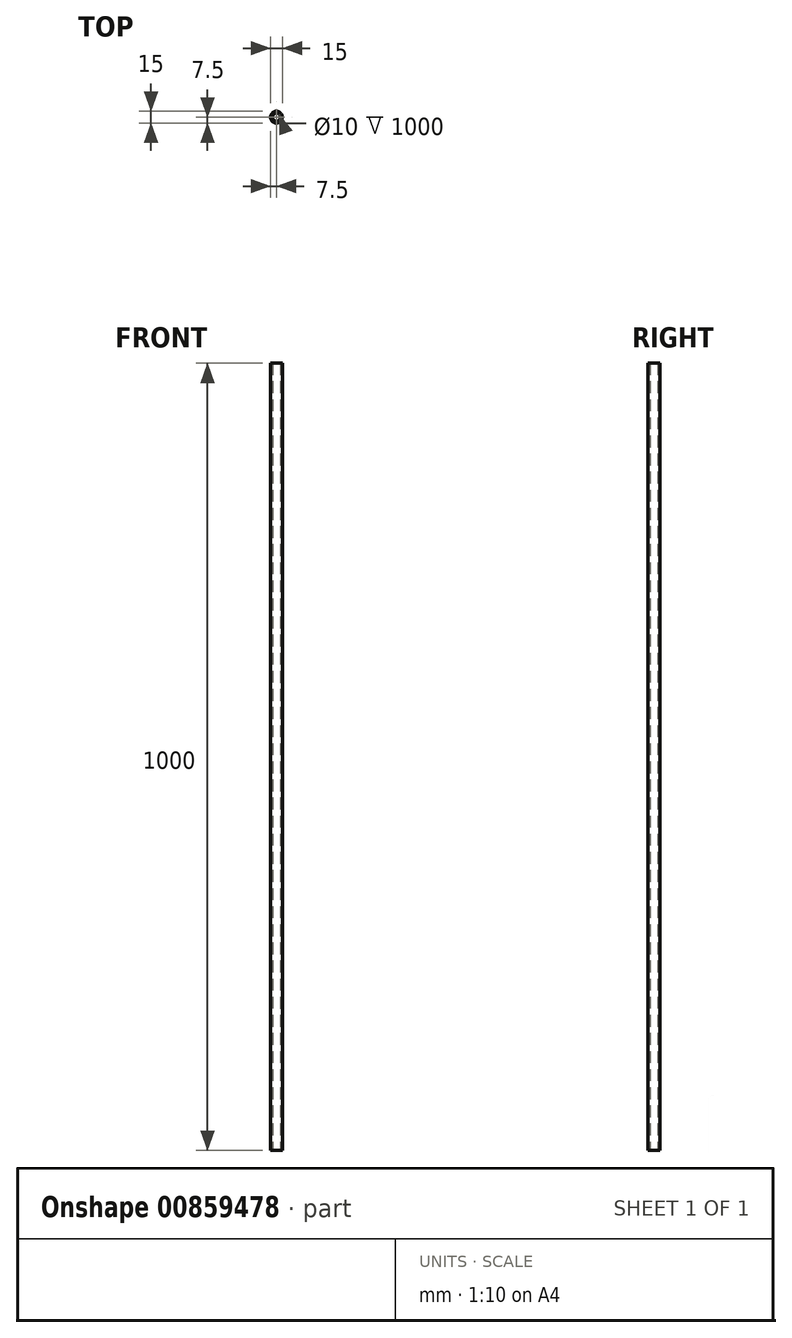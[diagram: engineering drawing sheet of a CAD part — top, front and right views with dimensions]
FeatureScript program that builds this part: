
annotation { "Feature Type Name" : "Feature", "Feature Type Description" : "" }
export const myFeature = defineFeature(function(context is Context, id is Id, definition is map)
    precondition{}
    {
        {
            var Q0;
            Q0=qCreatedBy(makeId("Top.planeOp"),FACE);
            var sketch = newSketch(context, id + "F0", { "sketchPlane" : qUnion([Q0])});
            skCircle(sketch, "E0", {"center": v(0, 0) * mm, "radius": 7.5 * mm});
            skSolve(sketch);
        }
        {
            var Q0;
            Q0 = qSketchRegion(id + "F0", true);
            extrude(context, id + "F1", {"entities" : qUnion([Q0]), "endBound" : BoundingType.SYMMETRIC, "depth" : 1000 * mm, "offsetDistance" : 25 * mm});
        }
        {
            var Q0;
            Q0=qCreatedBy(makeId("Top.planeOp"),FACE);
            var sketch = newSketch(context, id + "F2", { "sketchPlane" : qUnion([Q0])});
            skCircle(sketch, "E1", {"center": v(0, 0) * mm, "radius": 5 * mm});
            skSolve(sketch);
        }
        {
            var Q0;
            Q0 = qSketchRegion(id + "F2", true);
            extrude(context, id + "F3", {"entities" : qUnion([Q0]), "operationType" : NewBodyOperationType.REMOVE, "endBound" : BoundingType.SYMMETRIC, "depth" : 1000 * mm, "offsetDistance" : 25 * mm});
        }
        {
            var Q0;
            Q0=qCreatedBy(makeId("Top.planeOp"),FACE);
            cPlane(context, id + "F4", {"entities" : qUnion([Q0]), "cplaneType" : CPlaneType.OFFSET, "offset" : 455 * mm, "width" : 150 * mm, "height" : 150 * mm});
        }
    });
